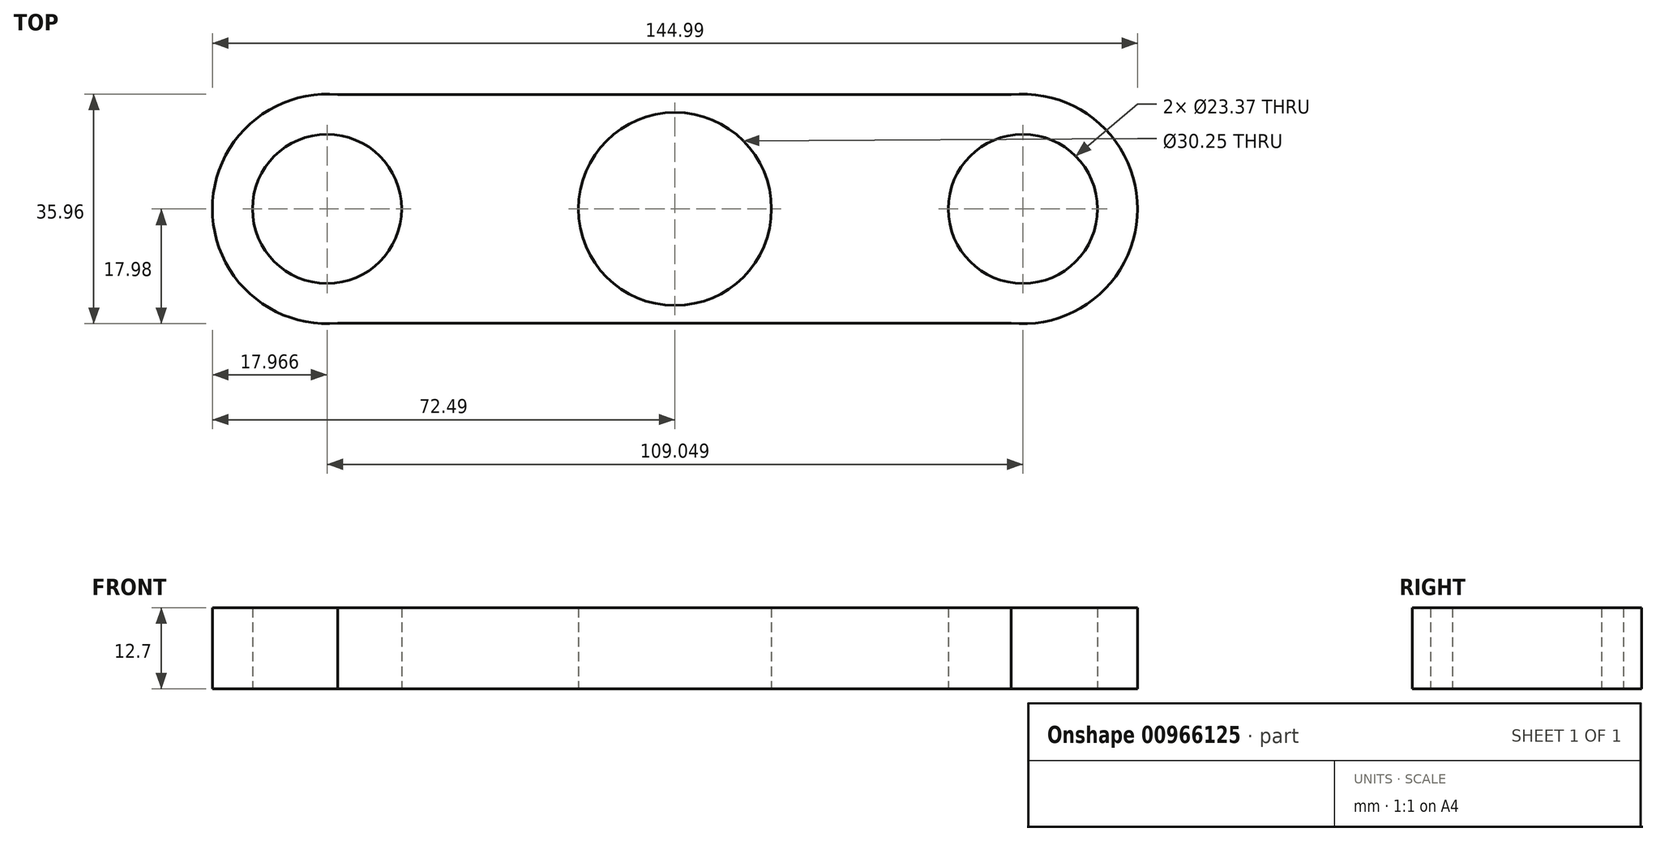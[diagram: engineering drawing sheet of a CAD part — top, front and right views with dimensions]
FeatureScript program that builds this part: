
annotation { "Feature Type Name" : "Feature", "Feature Type Description" : "" }
export const myFeature = defineFeature(function(context is Context, id is Id, definition is map)
    precondition{}
    {
        {
            var Q0;
            Q0=qCreatedBy(makeId("Top.planeOp"),FACE);
            var sketch = newSketch(context, id + "F0", { "sketchPlane" : qUnion([Q0])});
            skLineSegment(sketch, "E0.bottom", {"start": v(54.52, 17.89) * mm, "end": v(-54.52, 17.89) * mm});
            skLineSegment(sketch, "E0.top", {"start": v(54.52, -17.89) * mm, "end": v(-54.52, -17.89) * mm});
            skPoint(sketch, "E0.middle", {"position": v(0, 0) * mm});
            skArc(sketch, "E1", {"start": v(54.52, -17.89) * mm, "mid": v(72.41, 0) * mm, "end": v(54.52, 17.89) * mm});
            skArc(sketch, "E2", {"start": v(-54.52, 17.89) * mm, "mid": v(-72.41, 0) * mm, "end": v(-54.52, -17.89) * mm});
            skArc(sketch, "E3", {"start": v(-52.83, 17.89) * mm, "mid": v(-72.5, 0) * mm, "end": v(-52.83, -17.89) * mm});
            skArc(sketch, "E4", {"start": v(52.71, -17.89) * mm, "mid": v(72.5, 0) * mm, "end": v(52.71, 17.89) * mm});
            skCircle(sketch, "E5", {"center": v(0, 0) * mm, "radius": 15.13 * mm});
            skCircle(sketch, "E6", {"center": v(-54.52, 0) * mm, "radius": 11.69 * mm});
            skCircle(sketch, "E7", {"center": v(54.52, 0) * mm, "radius": 11.69 * mm});
            skSolve(sketch);
        }
        {
            var Q0;
            {var subQ0=sQuery(id+"F0.wireOp",EDGE,"E1");Q0=makeQuery(id+"F0.imprint","IMPRINT",FACE,{"disambiguationData":[TD([[makeQuery(id+"F0.imprint","IMPRINT",EDGE,{"derivedFrom":subQ0}),-1.0]])]});}
            var Q1;
            {var subQ0=sQuery(id+"F0.wireOp",EDGE,"E2");Q1=makeQuery(id+"F0.imprint","IMPRINT",FACE,{"disambiguationData":[TD([[makeQuery(id+"F0.imprint","IMPRINT",EDGE,{"derivedFrom":subQ0}),-1.0]])]});}
            var Q2;
            {var subQ1=sQuery(id+"F0.wireOp",EDGE,"E1");Q2=makeQuery(id+"F0.imprint","IMPRINT",FACE,{"disambiguationData":[TD([[makeQuery(id+"F0.imprint","IMPRINT",EDGE,{"derivedFrom":subQ1}),1.0]])]});}
            extrude(context, id + "F1", {"entities" : qUnion([Q0, Q1, Q2]), "depth" : 12.7 * mm, "offsetDistance" : 25.4 * mm});
        }
    });
